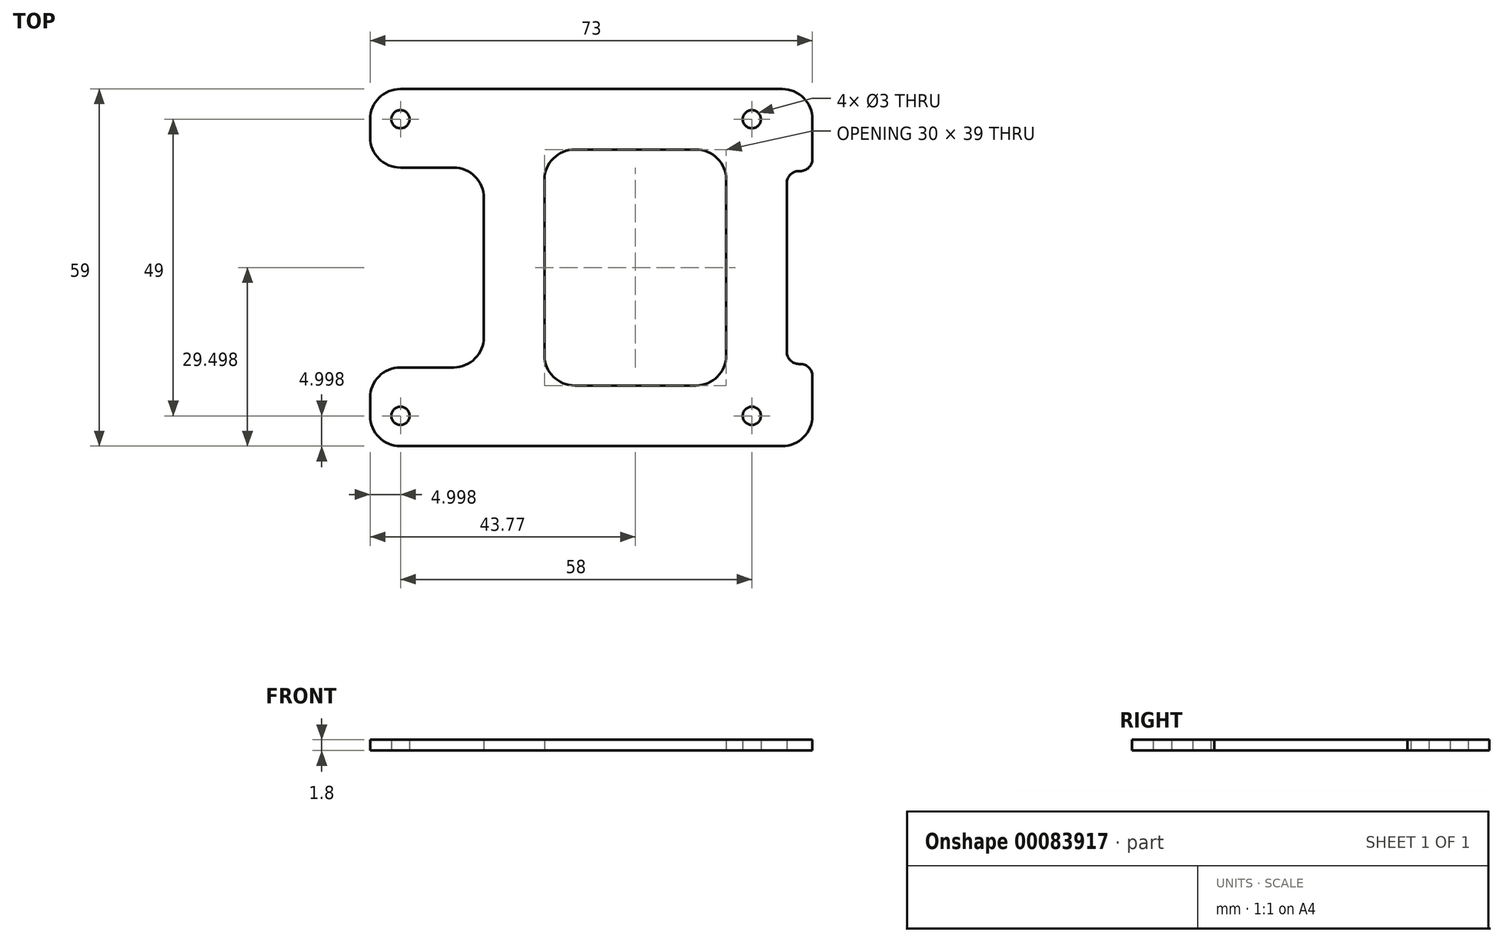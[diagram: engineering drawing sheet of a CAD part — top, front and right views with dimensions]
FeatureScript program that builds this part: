
annotation { "Feature Type Name" : "Feature", "Feature Type Description" : "" }
export const myFeature = defineFeature(function(context is Context, id is Id, definition is map)
    precondition{}
    {
        {
            var Q0;
            Q0=qCreatedBy(makeId("Top.planeOp"),FACE);
            var sketch = newSketch(context, id + "F0", { "sketchPlane" : qUnion([Q0])});
            skLineSegment(sketch, "E0.bottom", {"start": v(-30.44, 27.96) * mm, "end": v(27.56, 27.96) * mm, "construction": true});
            skLineSegment(sketch, "E0.top", {"start": v(-30.44, -21.04) * mm, "end": v(27.56, -21.04) * mm, "construction": true});
            skLineSegment(sketch, "E0.left", {"start": v(-30.44, 27.96) * mm, "end": v(-30.44, -21.04) * mm, "construction": true});
            skLineSegment(sketch, "E0.right", {"start": v(27.56, 27.96) * mm, "end": v(27.56, -21.04) * mm, "construction": true});
            skCircle(sketch, "E1", {"center": v(27.56, 27.96) * mm, "radius": 1.5 * mm, "construction": true});
            skCircle(sketch, "E2.2.0.0", {"center": v(127.56, 27.96) * mm, "radius": 1 * mm, "construction": true});
            skCircle(sketch, "E3", {"center": v(-30.44, 27.96) * mm, "radius": 1.5 * mm, "construction": true});
            skCircle(sketch, "E4", {"center": v(-30.44, -21.04) * mm, "radius": 1.5 * mm, "construction": true});
            skCircle(sketch, "E5", {"center": v(27.56, -21.04) * mm, "radius": 1.5 * mm, "construction": true});
            skSolve(sketch);
        }
        {
            var Q0;
            Q0=qCreatedBy(makeId("Top.planeOp"),FACE);
            var sketch = newSketch(context, id + "F1", { "sketchPlane" : qUnion([Q0])});
            skLineSegment(sketch, "E6.bottom", {"start": v(-35.44, -26.04) * mm, "end": v(37.56, -26.04) * mm, "construction": true});
            skLineSegment(sketch, "E6.top", {"start": v(-35.44, 32.96) * mm, "end": v(37.56, 32.96) * mm, "construction": true});
            skLineSegment(sketch, "E6.left", {"start": v(-35.44, -26.04) * mm, "end": v(-35.44, 32.96) * mm, "construction": true});
            skLineSegment(sketch, "E6.right", {"start": v(37.56, -26.04) * mm, "end": v(37.56, 32.96) * mm, "construction": true});
            skLineSegment(sketch, "E7", {"start": v(-35.44, 3.46) * mm, "end": v(-30.44, 3.46) * mm, "construction": true});
            skLineSegment(sketch, "E8", {"start": v(-10.17, 32.96) * mm, "end": v(-10.17, 27.96) * mm, "construction": true});
            skLineSegment(sketch, "E9", {"start": v(-10.85, -26.04) * mm, "end": v(-10.85, -21.04) * mm, "construction": true});
            skSolve(sketch);
        }
        {
            var Q0;
            Q0=qCreatedBy(makeId("Top.planeOp"),FACE);
            var sketch = newSketch(context, id + "F2", { "sketchPlane" : qUnion([Q0])});
            skLineSegment(sketch, "E10.0", {"start": v(-35.44, 32.96) * mm, "end": v(37.56, 32.96) * mm});
            skLineSegment(sketch, "E11.0", {"start": v(-35.44, -26.04) * mm, "end": v(37.56, -26.04) * mm});
            skCircle(sketch, "E12.0", {"center": v(-30.44, -21.04) * mm, "radius": 1.5 * mm});
            skCircle(sketch, "E13.0", {"center": v(-30.44, 27.96) * mm, "radius": 1.5 * mm});
            skCircle(sketch, "E14.0", {"center": v(27.56, -21.04) * mm, "radius": 1.5 * mm});
            skCircle(sketch, "E14.1", {"center": v(27.56, 27.96) * mm, "radius": 1.5 * mm});
            skLineSegment(sketch, "E15", {"start": v(-35.44, -26.04) * mm, "end": v(-35.44, -13.04) * mm});
            skLineSegment(sketch, "E16", {"start": v(-16.67, -13.04) * mm, "end": v(-35.44, -13.04) * mm});
            skLineSegment(sketch, "E17", {"start": v(-35.44, 32.96) * mm, "end": v(-35.44, 19.96) * mm});
            skLineSegment(sketch, "E18", {"start": v(-16.67, 19.96) * mm, "end": v(-35.44, 19.96) * mm});
            skLineSegment(sketch, "E19.bottom", {"start": v(-6.67, 22.96) * mm, "end": v(23.33, 22.96) * mm});
            skLineSegment(sketch, "E19.top", {"start": v(-6.67, -16.04) * mm, "end": v(23.33, -16.04) * mm});
            skLineSegment(sketch, "E19.left", {"start": v(-6.67, 22.96) * mm, "end": v(-6.67, -16.04) * mm});
            skLineSegment(sketch, "E19.right", {"start": v(23.33, 22.96) * mm, "end": v(23.33, -16.04) * mm});
            skPoint(sketch, "E19.middle", {"position": v(8.33, 3.46) * mm});
            skLineSegment(sketch, "E20", {"start": v(33.33, 19.4) * mm, "end": v(37.56, 19.4) * mm});
            skLineSegment(sketch, "E21.trimOffspring", {"start": v(37.56, 19.4) * mm, "end": v(37.56, 32.96) * mm});
            skLineSegment(sketch, "E22", {"start": v(-16.67, 19.96) * mm, "end": v(-16.67, -13.04) * mm});
            skLineSegment(sketch, "E23", {"start": v(33.33, 19.4) * mm, "end": v(33.33, -12.48) * mm});
            skLineSegment(sketch, "E24.0", {"start": v(37.56, -26.04) * mm, "end": v(37.56, 32.96) * mm, "construction": true});
            skLineSegment(sketch, "E25", {"start": v(33.33, -12.48) * mm, "end": v(37.56, -12.48) * mm});
            skLineSegment(sketch, "E26", {"start": v(37.56, -12.48) * mm, "end": v(37.56, -26.04) * mm});
            skSolve(sketch);
        }
        {
            var Q0;
            Q0=makeQuery(id+"F2.imprint","IMPRINT",FACE,{"disambiguationData":[TD([[makeQuery(id+"F2.imprint","IMPRINT",EDGE,{"derivedFrom":sQuery(id+"F2.wireOp",EDGE,"E10.0")}),-1.0]])]});
            extrude(context, id + "F3", {"entities" : qUnion([Q0]), "depth" : 1.8 * mm});
        }
        {
            var Q0;
            Q0=makeQuery(id+"F3.opExtrude","CAP_FACE",FACE,{"disambiguationData":[OSD([sQuery(id+"F2.wireOp",EDGE,"E10.0"),sQuery(id+"F2.wireOp",EDGE,"E11.0"),sQuery(id+"F2.wireOp",EDGE,"2da4875d-c075-4c1f-bcd7-1f953fda9f2d.0"),sQuery(id+"F2.wireOp",EDGE,"Bsazm0Rl-HW6d-kQB3-EfzJ-pV1Ywl2nqT3g"),sQuery(id+"F2.wireOp",EDGE,"4mQzWqNt-KW6x-kREw-m6Hx-6bZFHgzOOl8B"),sQuery(id+"F2.wireOp",EDGE,"wW12KO5x-R8PX-ogSw-A3dy-AmjbothRXtzv"),sQuery(id+"F2.wireOp",EDGE,"YNJuHpAd-y7u7-mqO4-l4rb-sBYpDEALbsT5"),sQuery(id+"F2.wireOp",EDGE,"dfac7e03-bceb-41b9-bd98-0e31ba661a0a.trimOffspring"),sQuery(id+"F2.wireOp",EDGE,"2682c02b-dc11-432b-bda7-b61fb366b2400.MirrorCS"),sQuery(id+"F2.wireOp",EDGE,"943b185a-d7e3-4790-a87f-9ef3a896942d0.MirrorCS"),sQuery(id+"F2.wireOp",EDGE,"fc1fbf68-c535-4f17-9666-a37acd9e6c940.MirrorCS"),sQuery(id+"F2.wireOp",EDGE,"fcaa26ce-abeb-4e5f-8a9f-b06a84bd164d0.MirrorCS"),sQuery(id+"F2.wireOp",EDGE,"ce83218e-15ea-4675-9c7a-5a9dfb48313d.0"),sQuery(id+"F2.wireOp",EDGE,"60752826-4fac-4f77-bb67-37b13a98344f.0"),sQuery(id+"F2.wireOp",EDGE,"JZ4oTpcl-TPOe-aru8-cmRJ-1lebC6cK4Rik"),sQuery(id+"F2.wireOp",EDGE,"U1Yn7I4e-NzDn-3yl1-5NNj-qfT3pnWFEAUy"),sQuery(id+"F2.wireOp",EDGE,"09ba057e-26f9-4483-8f59-dfd9f0267ff7.trimOffspring")])],"isStart":false});
            var sketch = newSketch(context, id + "F4", { "sketchPlane" : qUnion([Q0])});
            skCircle(sketch, "E27.0", {"center": v(-30.44, 27.96) * mm, "radius": 1.5 * mm});
            skCircle(sketch, "E28.0", {"center": v(27.56, 27.96) * mm, "radius": 1.5 * mm});
            skCircle(sketch, "E29.0", {"center": v(27.56, -21.04) * mm, "radius": 1.5 * mm});
            skCircle(sketch, "E30.0", {"center": v(-30.44, -21.04) * mm, "radius": 1.5 * mm});
            skCircle(sketch, "E31", {"center": v(-30.44, 27.96) * mm, "radius": 3.1 * mm});
            skCircle(sketch, "E32", {"center": v(-30.44, -21.04) * mm, "radius": 3.1 * mm});
            skCircle(sketch, "E33", {"center": v(27.56, -21.04) * mm, "radius": 3.1 * mm});
            skCircle(sketch, "E34", {"center": v(27.56, 27.96) * mm, "radius": 3.1 * mm});
            skSolve(sketch);
        }
        {
            var Q0;
            Q0=makeQuery(id+"F3.opExtrude","SWEPT_EDGE",EDGE,{"disambiguationData":[OSD([sQuery(id+"F2.wireOp",EDGE,"E19.bottom"),sQuery(id+"F2.wireOp",EDGE,"E19.left")])]});
            var Q1;
            Q1=makeQuery(id+"F3.opExtrude","SWEPT_EDGE",EDGE,{"disambiguationData":[OSD([sQuery(id+"F2.wireOp",EDGE,"E19.top"),sQuery(id+"F2.wireOp",EDGE,"E19.left")])]});
            var Q2;
            Q2=makeQuery(id+"F3.opExtrude","SWEPT_EDGE",EDGE,{"disambiguationData":[OSD([sQuery(id+"F2.wireOp",EDGE,"E19.top"),sQuery(id+"F2.wireOp",EDGE,"E19.right")])]});
            var Q3;
            Q3=makeQuery(id+"F3.opExtrude","SWEPT_EDGE",EDGE,{"disambiguationData":[OSD([sQuery(id+"F2.wireOp",EDGE,"E19.bottom"),sQuery(id+"F2.wireOp",EDGE,"E19.right")])]});
            var Q4;
            Q4=makeQuery(id+"F3.opExtrude","SWEPT_EDGE",EDGE,{"disambiguationData":[OSD([sQuery(id+"F2.wireOp",EDGE,"E11.0"),sQuery(id+"F2.wireOp",EDGE,"2da4875d-c075-4c1f-bcd7-1f953fda9f2d.0")])]});
            var Q5;
            Q5=makeQuery(id+"F3.opExtrude","SWEPT_EDGE",EDGE,{"disambiguationData":[OSD([sQuery(id+"F2.wireOp",EDGE,"E10.0"),sQuery(id+"F2.wireOp",EDGE,"E21.trimOffspring")])]});
            var Q6;
            Q6=makeQuery(id+"F3.opExtrude","SWEPT_EDGE",EDGE,{"disambiguationData":[OSD([sQuery(id+"F2.wireOp",EDGE,"E11.0"),sQuery(id+"F2.wireOp",EDGE,"E15")])]});
            var Q7;
            Q7=makeQuery(id+"F3.opExtrude","SWEPT_EDGE",EDGE,{"disambiguationData":[OSD([sQuery(id+"F2.wireOp",EDGE,"E10.0"),sQuery(id+"F2.wireOp",EDGE,"E17")])]});
            var Q8;
            Q8=makeQuery(id+"F3.opExtrude","SWEPT_EDGE",EDGE,{"disambiguationData":[OSD([sQuery(id+"F2.wireOp",EDGE,"E16"),sQuery(id+"F2.wireOp",EDGE,"E22")])]});
            var Q9;
            Q9=makeQuery(id+"F3.opExtrude","SWEPT_EDGE",EDGE,{"disambiguationData":[OSD([sQuery(id+"F2.wireOp",EDGE,"E18"),sQuery(id+"F2.wireOp",EDGE,"E22")])]});
            var Q10;
            Q10=makeQuery(id+"F3.opExtrude","SWEPT_EDGE",EDGE,{"disambiguationData":[OSD([sQuery(id+"F2.wireOp",EDGE,"E17"),sQuery(id+"F2.wireOp",EDGE,"E18")])]});
            var Q11;
            Q11=makeQuery(id+"F3.opExtrude","SWEPT_EDGE",EDGE,{"disambiguationData":[OSD([sQuery(id+"F2.wireOp",EDGE,"E15"),sQuery(id+"F2.wireOp",EDGE,"E16")])]});
            fillet(context, id + "F5", {"entities" : qUnion([Q0, Q1, Q2, Q3, Q4, Q5, Q6, Q7, Q8, Q9, Q10, Q11]), "radius" : 5 * mm, "tangentPropagation" : true, "allowEdgeOverflow" : false});
        }
        {
            var Q0;
            Q0=makeQuery(id+"F3.opExtrude","SWEPT_EDGE",EDGE,{"disambiguationData":[OSD([sQuery(id+"F2.wireOp",EDGE,"E20"),sQuery(id+"F2.wireOp",EDGE,"E21.trimOffspring")])]});
            var Q1;
            Q1=makeQuery(id+"F3.opExtrude","SWEPT_EDGE",EDGE,{"disambiguationData":[OSD([sQuery(id+"F2.wireOp",EDGE,"E25"),sQuery(id+"F2.wireOp",EDGE,"E26")])]});
            var Q2;
            Q2=makeQuery(id+"F3.opExtrude","SWEPT_EDGE",EDGE,{"disambiguationData":[OSD([sQuery(id+"F2.wireOp",EDGE,"E20"),sQuery(id+"F2.wireOp",EDGE,"E23")])]});
            var Q3;
            Q3=makeQuery(id+"F3.opExtrude","SWEPT_EDGE",EDGE,{"disambiguationData":[OSD([sQuery(id+"F2.wireOp",EDGE,"E23"),sQuery(id+"F2.wireOp",EDGE,"E25")])]});
            fillet(context, id + "F6", {"entities" : qUnion([Q0, Q1, Q2, Q3]), "radius" : 2 * mm, "tangentPropagation" : true, "allowEdgeOverflow" : false});
        }
    });
